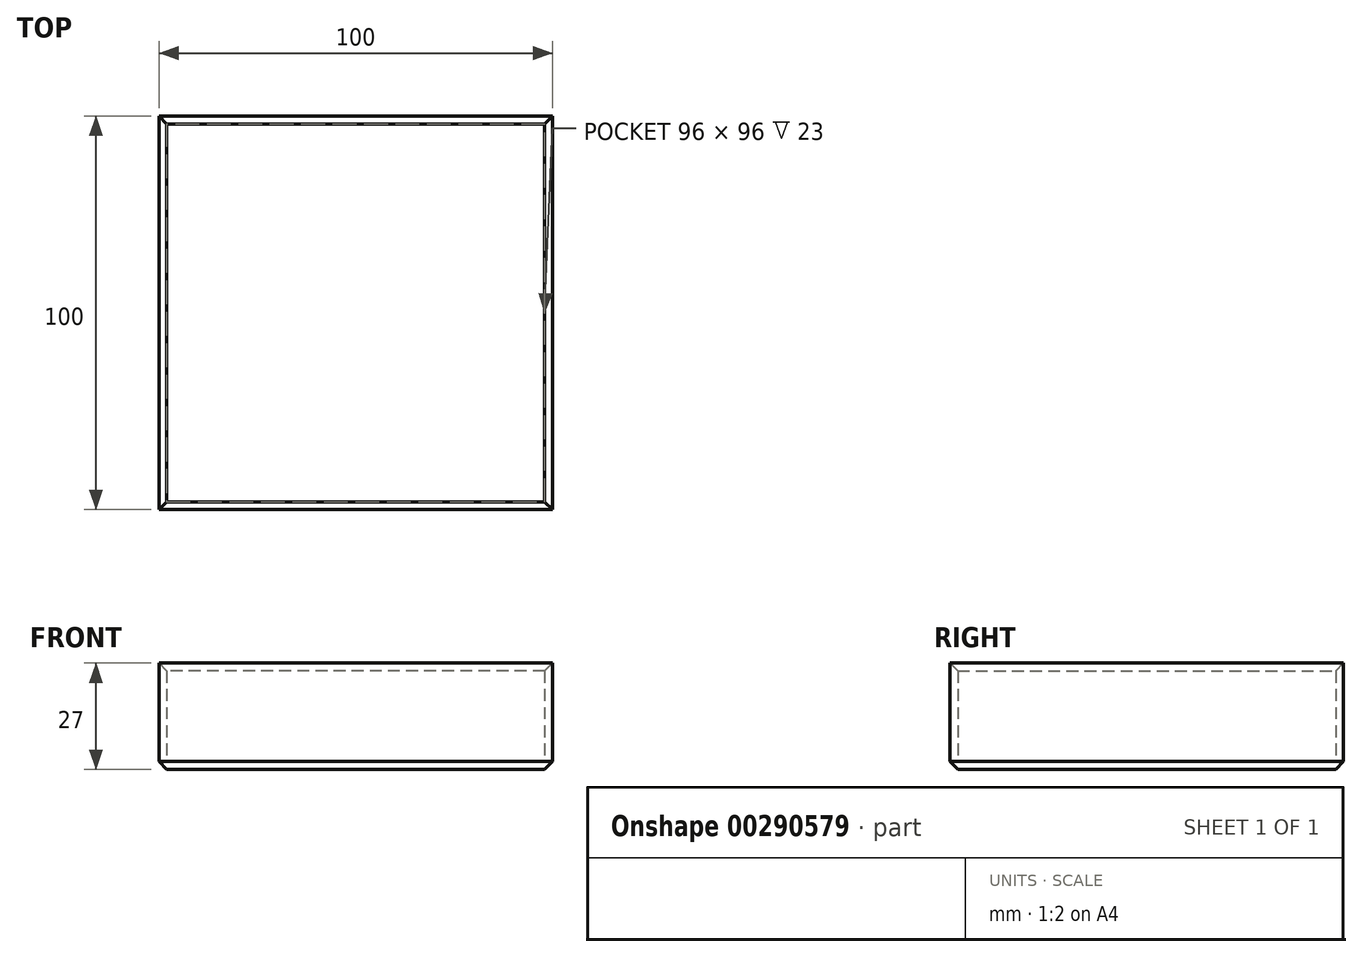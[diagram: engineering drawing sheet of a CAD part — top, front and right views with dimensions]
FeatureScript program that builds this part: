
annotation { "Feature Type Name" : "Feature", "Feature Type Description" : "" }
export const myFeature = defineFeature(function(context is Context, id is Id, definition is map)
    precondition{}
    {
        {
            var Q0;
            Q0=qCreatedBy(makeId("Top.planeOp"),FACE);
            var sketch = newSketch(context, id + "F0", { "sketchPlane" : qUnion([Q0])});
            skLineSegment(sketch, "E0.bottom", {"start": v(50, 50) * mm, "end": v(-50, 50) * mm});
            skLineSegment(sketch, "E0.top", {"start": v(50, -50) * mm, "end": v(-50, -50) * mm});
            skLineSegment(sketch, "E0.left", {"start": v(50, 50) * mm, "end": v(50, -50) * mm});
            skLineSegment(sketch, "E0.right", {"start": v(-50, 50) * mm, "end": v(-50, -50) * mm});
            skPoint(sketch, "E0.middle", {"position": v(0, 0) * mm});
            skLineSegment(sketch, "E1.0", {"start": v(48, 48) * mm, "end": v(-48, 48) * mm});
            skLineSegment(sketch, "E1.1", {"start": v(48, 48) * mm, "end": v(48, -48) * mm});
            skLineSegment(sketch, "E1.2", {"start": v(48, -48) * mm, "end": v(-48, -48) * mm});
            skLineSegment(sketch, "E1.3", {"start": v(-48, 48) * mm, "end": v(-48, -48) * mm});
            skSolve(sketch);
        }
        {
            var Q0;
            Q0=makeQuery(id+"F0.imprint","IMPRINT",FACE,{"disambiguationData":[TD([[makeQuery(id+"F0.imprint","IMPRINT",EDGE,{"derivedFrom":sQuery(id+"F0.wireOp",EDGE,"E0.bottom")}),1.0]])]});
            extrude(context, id + "F1", {"entities" : qUnion([Q0]), "depth" : 25 * mm});
        }
        {
            var Q0;
            Q0 = qSketchRegion(id + "F0", true);
            var Q1;
            Q1=makeQuery(id+"F0.imprint","IMPRINT",FACE,{"disambiguationData":[TD([[makeQuery(id+"F0.imprint","IMPRINT",EDGE,{"derivedFrom":sQuery(id+"F0.wireOp",EDGE,"E1.0")}),1.0]])]});
            extrude(context, id + "F2", {"entities" : qUnion([Q0, Q1]), "operationType" : NewBodyOperationType.ADD, "oppositeDirection" : true, "depth" : 2 * mm});
        }
        {
            var Q0;
            Q0=makeQuery(id+"F2.opExtrude","CAP_EDGE",EDGE,{"disambiguationData":[OSD([sQuery(id+"F0.wireOp",EDGE,"E0.top")])],"isStart":false});
            var Q1;
            Q1=makeQuery(id+"F2.opExtrude","CAP_EDGE",EDGE,{"disambiguationData":[OSD([sQuery(id+"F0.wireOp",EDGE,"E0.right")])],"isStart":false});
            var Q2;
            Q2=makeQuery(id+"F2.opExtrude","CAP_EDGE",EDGE,{"disambiguationData":[OSD([sQuery(id+"F0.wireOp",EDGE,"E0.left")])],"isStart":false});
            var Q3;
            Q3=makeQuery(id+"F2.opExtrude","CAP_EDGE",EDGE,{"disambiguationData":[OSD([sQuery(id+"F0.wireOp",EDGE,"E0.bottom")])],"isStart":false});
            var Q4;
            Q4=makeQuery(id+"F1.opExtrude","CAP_EDGE",EDGE,{"disambiguationData":[OSD([sQuery(id+"F0.wireOp",EDGE,"E1.3")])],"isStart":false});
            var Q5;
            Q5=makeQuery(id+"F1.opExtrude","CAP_EDGE",EDGE,{"disambiguationData":[OSD([sQuery(id+"F0.wireOp",EDGE,"E1.0")])],"isStart":false});
            var Q6;
            Q6=makeQuery(id+"F1.opExtrude","CAP_EDGE",EDGE,{"disambiguationData":[OSD([sQuery(id+"F0.wireOp",EDGE,"E1.1")])],"isStart":false});
            var Q7;
            Q7=makeQuery(id+"F1.opExtrude","CAP_EDGE",EDGE,{"disambiguationData":[OSD([sQuery(id+"F0.wireOp",EDGE,"E1.2")])],"isStart":false});
            chamfer(context, id + "F3", {"entities" : qUnion([Q0, Q1, Q2, Q3, Q4, Q5, Q6, Q7]), "width" : 2 * mm, "tangentPropagation" : true});
        }
    });
